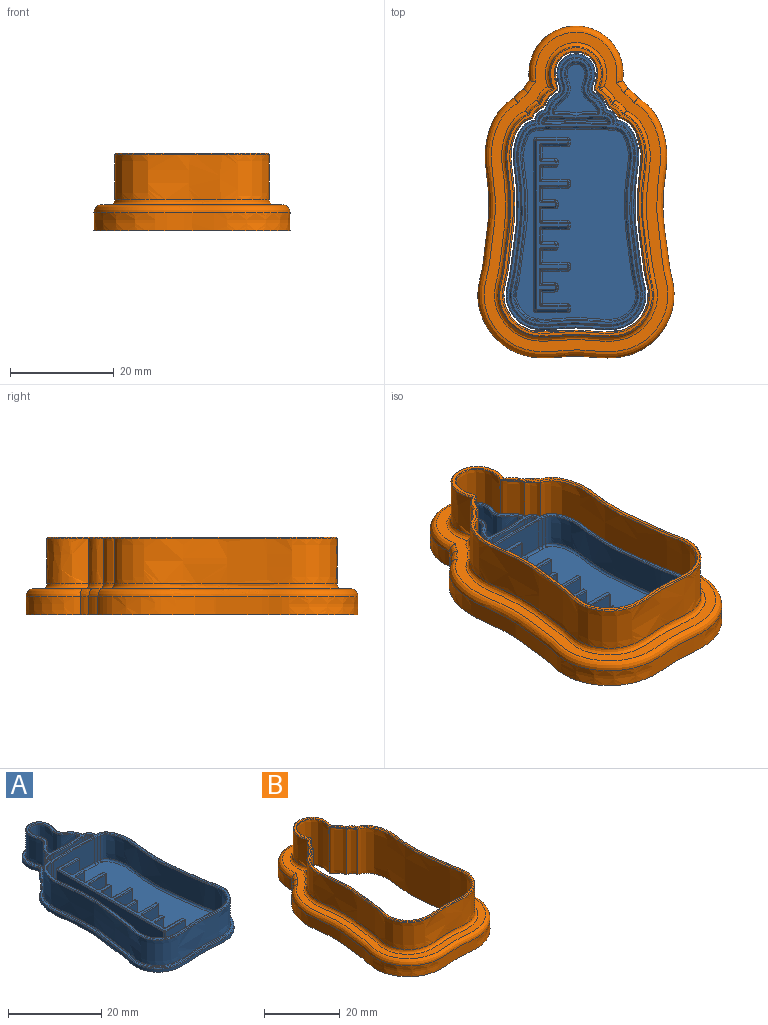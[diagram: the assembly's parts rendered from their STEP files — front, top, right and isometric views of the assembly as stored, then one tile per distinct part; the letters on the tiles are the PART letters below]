
ASSEMBLY  parts=2 mates=1
PART A: 339 faces, bbox 27.6x53.8x8.8 mm
  f0: plane 53.06x26.86mm, normal (0,0,1), area 61.6mm2, adj f215,f216,f217,f218,f219,f220,f221,f222
  f1: extruded ~2.03x1.99mm, area 2.4mm2, adj f2,f4,f5,f227
  f2: extruded ~12.02x10.77mm, area 22.5mm2, adj f1,f3,f5,f229
  f3: extruded ~2.03x1.99mm, area 2.4mm2, adj f2,f4,f5,f230
  f4: extruded ~40.24x26.6mm, area 85.2mm2, adj f1,f3,f5,f228
  f5: plane 53.17x26.93mm, normal (0,0,-1), area 1065.3mm2, adj f1,f2,f3,f4
  f6: extruded ~8.45x6.3mm, area 53.3mm2, adj f115,f118,f206,f234
  f7: extruded ~6.3x0.53mm, area 3.5mm2, adj f8,f118,f203,f235
  f8: extruded ~9.06x8.62mm, area 143.6mm2, adj f7,f37,f205,f233
  f9: extruded ~6.3x0.85mm, area 5.4mm2, adj f10,f34,f214,f334
  f10: extruded ~6.3x0.81mm, area 5.1mm2, adj f9,f11,f213,f333
  f11: extruded ~37.06x23.47mm, area 605.2mm2, adj f10,f12,f211,f335
  f12: extruded ~6.3x0.81mm, area 5.1mm2, adj f11,f13,f209,f337
  f13: extruded ~6.3x0.85mm, area 5.4mm2, adj f12,f34,f210,f338
  f14: extruded ~6.3x0.55mm, area 3.7mm2, adj f35,f116,f201,f242
  f15: extruded ~12.37x6.3mm, area 78mm2, adj f116,f117,f200,f246
  f16: extruded ~6.3x0.55mm, area 3.7mm2, adj f17,f117,f196,f247
  f17: extruded ~6.3x0.31mm, area 2.5mm2, adj f16,f18,f194,f245
  f18: extruded ~6.3x0.78mm, area 5.1mm2, adj f17,f19,f192,f243
  f19: extruded ~6.3x0.81mm, area 5.1mm2, adj f18,f20,f191,f241
  f20: extruded ~8.75x6.3mm, area 55.2mm2, adj f19,f21,f193,f239
  f21: extruded ~6.3x0.81mm, area 5.1mm2, adj f20,f22,f195,f237
  f22: extruded ~6.3x0.78mm, area 5.1mm2, adj f21,f35,f197,f238
  f23: extruded ~6.6x0.79mm, area 5.3mm2, adj f24,f36,f226,f324
  f24: extruded ~38.64x25.05mm, area 666.6mm2, adj f23,f25,f224,f322
  f25: extruded ~6.6x0.79mm, area 5.3mm2, adj f24,f26,f222,f321
  f26: extruded ~6.6x0.81mm, area 5.4mm2, adj f25,f27,f220,f323
  f27: extruded ~6.6x1.1mm, area 10.7mm2, adj f26,f28,f218,f325
  f28: extruded ~6.6x0.8mm, area 5.4mm2, adj f27,f29,f216,f327
  f29: extruded ~6.6x0.81mm, area 5.4mm2, adj f28,f30,f215,f329
  f30: extruded ~10.32x9.87mm, area 166.6mm2, adj f29,f31,f217,f331
  f31: extruded ~6.6x0.81mm, area 5.4mm2, adj f30,f32,f219,f332
  f32: extruded ~6.6x0.8mm, area 5.4mm2, adj f31,f33,f221,f330
  f33: extruded ~6.6x1.1mm, area 10.7mm2, adj f32,f36,f223,f328
  f34: extruded ~12.41x6.3mm, area 78.2mm2, adj f9,f13,f212,f336
  f35: extruded ~6.3x0.31mm, area 2.5mm2, adj f14,f22,f199,f240
  f36: extruded ~6.6x0.81mm, area 5.4mm2, adj f23,f33,f225,f326
  f37: extruded ~6.3x0.53mm, area 3.5mm2, adj f8,f115,f207,f231
  f38: plane 51.56x25.41mm, normal (0,0,1), area 70.5mm2, adj f231,f232,f233,f234,f235,f236,f237,f238
  f39: plane 12.32x0.72mm, normal (0,0,1), area 2.5mm2, adj f191,f192,f193,f194,f195,f196,f197,f199
  f40: plane 36.98x23.4mm, normal (0,0,1), area 599.8mm2, adj f120,f121,f123,f124,f125,f126,f127,f128
  f41: plane 9.88x8.66mm, normal (0,0,1), area 34.3mm2, adj f203,f205,f206,f207
  f42: plane 6.3x4.96mm, normal (0,1,0), area 31.2mm2, adj f79,f82,f172,f295
  f43: plane 6.3x2.56mm, normal (1,0,0), area 16.1mm2, adj f79,f84,f168,f291
  f44: plane 6.3x2.56mm, normal (0,-1,0), area 16.1mm2, adj f84,f85,f164,f287
  f45: plane 6.3x0.48mm, normal (1,0,0), area 3mm2, adj f85,f86,f160,f283
  f46: plane 6.3x2.56mm, normal (0,1,0), area 16.1mm2, adj f83,f86,f156,f279
  f47: plane 6.3x2.56mm, normal (1,0,0), area 16.1mm2, adj f83,f88,f152,f275
  f48: plane 6.3x4.96mm, normal (0,-1,0), area 31.2mm2, adj f88,f89,f148,f271
  f49: plane 6.3x0.48mm, normal (1,0,0), area 3mm2, adj f89,f90,f144,f267
  f50: plane 6.3x4.96mm, normal (0,1,0), area 31.2mm2, adj f87,f90,f140,f263
  f51: plane 6.3x2.56mm, normal (1,0,0), area 16.1mm2, adj f87,f91,f136,f259
  f52: plane 6.3x2.56mm, normal (0,-1,0), area 16.1mm2, adj f91,f93,f132,f255
  f53: plane 6.3x0.48mm, normal (1,0,0), area 3mm2, adj f93,f94,f128,f251
  f54: plane 6.3x2.56mm, normal (0,1,0), area 16.1mm2, adj f92,f94,f124,f250
  f55: plane 6.3x2.56mm, normal (1,0,0), area 16.1mm2, adj f92,f95,f120,f254
  f56: plane 6.3x4.96mm, normal (0,-1,0), area 31.2mm2, adj f95,f97,f121,f258
  f57: plane 6.3x0.48mm, normal (1,0,0), area 3mm2, adj f97,f98,f125,f262
  f58: plane 6.3x4.96mm, normal (0,1,0), area 31.2mm2, adj f96,f98,f129,f266
  f59: plane 6.3x2.56mm, normal (1,0,0), area 16.1mm2, adj f96,f99,f133,f270
  f60: plane 6.3x2.56mm, normal (0,-1,0), area 16.1mm2, adj f99,f101,f137,f274
  f61: plane 6.3x0.48mm, normal (1,0,0), area 3mm2, adj f101,f102,f141,f278
  f62: plane 6.3x2.56mm, normal (0,1,0), area 16.1mm2, adj f100,f102,f145,f282
  f63: plane 6.3x2.56mm, normal (1,0,0), area 16.1mm2, adj f100,f103,f149,f286
  f64: plane 6.3x4.96mm, normal (0,-1,0), area 31.2mm2, adj f103,f105,f153,f290
  f65: plane 6.3x0.48mm, normal (1,0,0), area 3mm2, adj f105,f106,f157,f294
  f66: plane 6.3x4.96mm, normal (0,1,0), area 31.2mm2, adj f104,f106,f161,f298
  f67: plane 6.3x2.56mm, normal (1,0,0), area 16.1mm2, adj f104,f107,f165,f302
  f68: plane 6.3x2.56mm, normal (0,-1,0), area 16.1mm2, adj f107,f109,f169,f306
  f69: plane 6.3x0.48mm, normal (1,0,0), area 3mm2, adj f109,f110,f173,f310
  f70: plane 6.3x2.56mm, normal (0,1,0), area 16.1mm2, adj f108,f110,f177,f314
  f71: plane 6.3x2.56mm, normal (1,0,0), area 16.1mm2, adj f108,f112,f181,f318
  f72: plane 6.3x4.96mm, normal (0,-1,0), area 31.2mm2, adj f112,f113,f185,f319
  f73: plane 6.3x0.48mm, normal (1,0,0), area 3mm2, adj f113,f114,f189,f315
  f74: plane 6.3x5.92mm, normal (0,1,0), area 37.3mm2, adj f111,f114,f188,f311
  f75: plane 32.48x6.3mm, normal (-1,0,0), area 204.6mm2, adj f80,f111,f184,f307
  f76: plane 6.3x5.92mm, normal (0,-1,0), area 37.3mm2, adj f80,f81,f180,f303
  f77: plane 6.3x0.48mm, normal (1,0,0), area 3mm2, adj f81,f82,f176,f299
  f78: plane 32.75x6.19mm, normal (0,0,1), area 46.6mm2, adj f249,f250,f251,f252,f253,f254,f255,f256
  f79: cylinder r=0.24mm len=6.3mm, axis (0,0,1), area 2.4mm2, adj f42,f43,f170,f293
  f80: cylinder r=0.24mm len=6.3mm, axis (0,0,-1), area 2.4mm2, adj f75,f76,f182,f305
  f81: cylinder r=0.24mm len=6.3mm, axis (0,0,-1), area 2.4mm2, adj f76,f77,f178,f301
  f82: cylinder r=0.24mm len=6.3mm, axis (0,0,-1), area 2.4mm2, adj f42,f77,f174,f297
  f83: cylinder r=0.24mm len=6.3mm, axis (0,0,1), area 2.4mm2, adj f46,f47,f154,f277
  f84: cylinder r=0.24mm len=6.3mm, axis (0,0,1), area 2.4mm2, adj f43,f44,f166,f289
  f85: cylinder r=0.24mm len=6.3mm, axis (0,0,-1), area 2.4mm2, adj f44,f45,f162,f285
  f86: cylinder r=0.24mm len=6.3mm, axis (0,0,-1), area 2.4mm2, adj f45,f46,f158,f281
  f87: cylinder r=0.24mm len=6.3mm, axis (0,0,1), area 2.4mm2, adj f50,f51,f138,f261
  f88: cylinder r=0.24mm len=6.3mm, axis (0,0,1), area 2.4mm2, adj f47,f48,f150,f273
  f89: cylinder r=0.24mm len=6.3mm, axis (0,0,-1), area 2.4mm2, adj f48,f49,f146,f269
  f90: cylinder r=0.24mm len=6.3mm, axis (0,0,-1), area 2.4mm2, adj f49,f50,f142,f265
  f91: cylinder r=0.24mm len=6.3mm, axis (0,0,1), area 2.4mm2, adj f51,f52,f134,f257
  f92: cylinder r=0.24mm len=6.3mm, axis (0,0,1), area 2.4mm2, adj f54,f55,f122,f252
  f93: cylinder r=0.24mm len=6.3mm, axis (0,0,-1), area 2.4mm2, adj f52,f53,f130,f253
  f94: cylinder r=0.24mm len=6.3mm, axis (0,0,-1), area 2.4mm2, adj f53,f54,f126,f249
  f95: cylinder r=0.24mm len=6.3mm, axis (0,0,1), area 2.4mm2, adj f55,f56,f119,f256
  f96: cylinder r=0.24mm len=6.3mm, axis (0,0,1), area 2.4mm2, adj f58,f59,f131,f268
  f97: cylinder r=0.24mm len=6.3mm, axis (0,0,-1), area 2.4mm2, adj f56,f57,f123,f260
  f98: cylinder r=0.24mm len=6.3mm, axis (0,0,-1), area 2.4mm2, adj f57,f58,f127,f264
  f99: cylinder r=0.24mm len=6.3mm, axis (0,0,1), area 2.4mm2, adj f59,f60,f135,f272
  f100: cylinder r=0.24mm len=6.3mm, axis (0,0,1), area 2.4mm2, adj f62,f63,f147,f284
  f101: cylinder r=0.24mm len=6.3mm, axis (0,0,-1), area 2.4mm2, adj f60,f61,f139,f276
  f102: cylinder r=0.24mm len=6.3mm, axis (0,0,-1), area 2.4mm2, adj f61,f62,f143,f280
  f103: cylinder r=0.24mm len=6.3mm, axis (0,0,1), area 2.4mm2, adj f63,f64,f151,f288
  f104: cylinder r=0.24mm len=6.3mm, axis (0,0,-1), area 2.4mm2, adj f66,f67,f163,f300
  f105: cylinder r=0.24mm len=6.3mm, axis (0,0,-1), area 2.4mm2, adj f64,f65,f155,f292
  f106: cylinder r=0.24mm len=6.3mm, axis (0,0,1), area 2.4mm2, adj f65,f66,f159,f296
  f107: cylinder r=0.24mm len=6.3mm, axis (0,0,1), area 2.4mm2, adj f67,f68,f167,f304
  f108: cylinder r=0.24mm len=6.3mm, axis (0,0,1), area 2.4mm2, adj f70,f71,f179,f316
  f109: cylinder r=0.24mm len=6.3mm, axis (0,0,-1), area 2.4mm2, adj f68,f69,f171,f308
  f110: cylinder r=0.24mm len=6.3mm, axis (0,0,-1), area 2.4mm2, adj f69,f70,f175,f312
  f111: cylinder r=0.24mm len=6.3mm, axis (0,0,-1), area 2.4mm2, adj f74,f75,f186,f309
  f112: cylinder r=0.24mm len=6.3mm, axis (0,0,1), area 2.4mm2, adj f71,f72,f183,f320
  f113: cylinder r=0.24mm len=6.3mm, axis (0,0,-1), area 2.4mm2, adj f72,f73,f187,f317
  f114: cylinder r=0.24mm len=6.3mm, axis (0,0,-1), area 2.4mm2, adj f73,f74,f190,f313
  f115: cylinder r=0.24mm len=6.3mm, axis (0,0,-1), area 2.5mm2, adj f6,f37,f208,f232
  f116: cylinder r=0.24mm len=6.3mm, axis (0,0,-1), area 2.5mm2, adj f14,f15,f202,f244
  f117: cylinder r=0.24mm len=6.3mm, axis (0,0,-1), area 2.5mm2, adj f15,f16,f198,f248
  f118: cylinder r=0.24mm len=6.3mm, axis (0,0,-1), area 2.5mm2, adj f6,f7,f204,f236
  f119: bspline ~0.5x0.4mm, area 0.1mm2, adj f95,f120,f121
  f120: extruded ~2.56x0.5mm, area 1.7mm2, adj f40,f55,f119,f122
  f121: extruded ~4.96x0.5mm, area 3.5mm2, adj f40,f56,f119,f123
  f122: bspline ~0.5x0.4mm, area 0.1mm2, adj f92,f120,f124
  f123: bspline ~2.08x2.08mm, area 0.4mm2, adj f40,f97,f121,f125
  f124: extruded ~2.56x0.5mm, area 1.8mm2, adj f40,f54,f122,f126
  f125: extruded ~0.5x0.48mm, area 0.3mm2, adj f40,f57,f123,f127
  f126: bspline ~2.08x2.08mm, area 0.4mm2, adj f40,f94,f124,f128
  f127: bspline ~2.08x2.08mm, area 0.4mm2, adj f40,f98,f125,f129
  f128: extruded ~0.5x0.48mm, area 0.3mm2, adj f40,f53,f126,f130
  f129: extruded ~4.96x0.5mm, area 3.5mm2, adj f40,f58,f127,f131
  f130: bspline ~2.08x2.08mm, area 0.4mm2, adj f40,f93,f128,f132
  f131: bspline ~0.5x0.4mm, area 0.1mm2, adj f96,f129,f133
  f132: extruded ~2.56x0.5mm, area 1.8mm2, adj f40,f52,f130,f134
  f133: extruded ~2.56x0.5mm, area 1.7mm2, adj f40,f59,f131,f135
  f134: bspline ~0.5x0.4mm, area 0.1mm2, adj f91,f132,f136
  f135: bspline ~0.5x0.4mm, area 0.1mm2, adj f99,f133,f137
  f136: extruded ~2.56x0.5mm, area 1.7mm2, adj f40,f51,f134,f138
  f137: extruded ~2.56x0.5mm, area 1.8mm2, adj f40,f60,f135,f139
  f138: bspline ~0.5x0.4mm, area 0.1mm2, adj f87,f136,f140
  f139: bspline ~2.08x2.08mm, area 0.4mm2, adj f40,f101,f137,f141
  f140: extruded ~4.96x0.5mm, area 3.5mm2, adj f40,f50,f138,f142
  f141: extruded ~0.5x0.48mm, area 0.3mm2, adj f40,f61,f139,f143
  f142: bspline ~2.08x2.08mm, area 0.4mm2, adj f40,f90,f140,f144
  f143: bspline ~2.08x2.08mm, area 0.4mm2, adj f40,f102,f141,f145
  f144: extruded ~0.5x0.48mm, area 0.3mm2, adj f40,f49,f142,f146
  f145: extruded ~2.56x0.5mm, area 1.8mm2, adj f40,f62,f143,f147
  f146: bspline ~2.08x2.08mm, area 0.4mm2, adj f40,f89,f144,f148
  f147: bspline ~0.5x0.4mm, area 0.1mm2, adj f100,f145,f149
  f148: extruded ~4.96x0.5mm, area 3.5mm2, adj f40,f48,f146,f150
  f149: extruded ~2.56x0.5mm, area 1.7mm2, adj f40,f63,f147,f151
  f150: bspline ~0.5x0.4mm, area 0.1mm2, adj f88,f148,f152
  f151: bspline ~0.5x0.4mm, area 0.1mm2, adj f103,f149,f153
  f152: extruded ~2.56x0.5mm, area 1.7mm2, adj f40,f47,f150,f154
  f153: extruded ~4.96x0.5mm, area 3.5mm2, adj f40,f64,f151,f155
  f154: bspline ~0.5x0.4mm, area 0.1mm2, adj f83,f152,f156
  f155: bspline ~2.08x2.08mm, area 0.4mm2, adj f40,f105,f153,f157
  f156: extruded ~2.56x0.5mm, area 1.8mm2, adj f40,f46,f154,f158
  f157: extruded ~0.5x0.48mm, area 0.3mm2, adj f40,f65,f155,f159
  f158: bspline ~2.08x2.08mm, area 0.4mm2, adj f40,f86,f156,f160
  f159: bspline ~2.08x2.08mm, area 0.4mm2, adj f40,f106,f157,f161
  f160: extruded ~0.5x0.48mm, area 0.3mm2, adj f40,f45,f158,f162
  f161: extruded ~4.96x0.5mm, area 3.5mm2, adj f40,f66,f159,f163
  f162: bspline ~2.08x2.08mm, area 0.4mm2, adj f40,f85,f160,f164
  f163: bspline ~0.5x0.4mm, area 0.1mm2, adj f104,f161,f165
  f164: extruded ~2.56x0.5mm, area 1.8mm2, adj f40,f44,f162,f166
  f165: extruded ~2.56x0.5mm, area 1.7mm2, adj f40,f67,f163,f167
  f166: bspline ~0.5x0.4mm, area 0.1mm2, adj f84,f164,f168
  f167: bspline ~0.5x0.4mm, area 0.1mm2, adj f107,f165,f169
  f168: extruded ~2.56x0.5mm, area 1.7mm2, adj f40,f43,f166,f170
  f169: extruded ~2.56x0.5mm, area 1.8mm2, adj f40,f68,f167,f171
  f170: bspline ~0.5x0.4mm, area 0.1mm2, adj f79,f168,f172
  f171: bspline ~2.08x2.08mm, area 0.4mm2, adj f40,f109,f169,f173
  f172: extruded ~4.96x0.5mm, area 3.5mm2, adj f40,f42,f170,f174
  f173: extruded ~0.5x0.48mm, area 0.3mm2, adj f40,f69,f171,f175
  f174: bspline ~2.08x2.08mm, area 0.4mm2, adj f40,f82,f172,f176
  f175: bspline ~2.08x2.08mm, area 0.4mm2, adj f40,f110,f173,f177
  f176: extruded ~0.5x0.48mm, area 0.3mm2, adj f40,f77,f174,f178
  f177: extruded ~2.56x0.5mm, area 1.8mm2, adj f40,f70,f175,f179
  f178: bspline ~2.08x2.08mm, area 0.4mm2, adj f40,f81,f176,f180
  f179: bspline ~0.5x0.4mm, area 0.1mm2, adj f108,f177,f181
  f180: extruded ~5.92x0.5mm, area 4.2mm2, adj f40,f76,f178,f182
  f181: extruded ~2.56x0.5mm, area 1.7mm2, adj f40,f71,f179,f183
  f182: bspline ~2.08x2.08mm, area 0.4mm2, adj f40,f80,f180,f184
  f183: bspline ~0.5x0.4mm, area 0.1mm2, adj f112,f181,f185
  f184: extruded ~32.48x0.5mm, area 23mm2, adj f40,f75,f182,f186
  f185: extruded ~4.96x0.5mm, area 3.5mm2, adj f40,f72,f183,f187
  f186: bspline ~2.08x2.08mm, area 0.4mm2, adj f40,f111,f184,f188
  f187: bspline ~2.08x2.08mm, area 0.4mm2, adj f40,f113,f185,f189
  f188: extruded ~5.92x0.5mm, area 4.2mm2, adj f40,f74,f186,f190
  f189: extruded ~0.5x0.48mm, area 0.3mm2, adj f40,f73,f187,f190
  f190: bspline ~2.08x2.08mm, area 0.4mm2, adj f40,f114,f188,f189
  f191: bspline ~0.81x0.5mm, area 0.6mm2, adj f19,f39,f192,f193
  f192: bspline ~0.81x0.53mm, area 0.5mm2, adj f18,f39,f191,f194
  f193: bspline ~8.76x0.61mm, area 6.2mm2, adj f20,f39,f191,f195
  f194: bspline ~0.5x0.48mm, area 0.2mm2, adj f17,f39,f192,f196
  f195: bspline ~0.81x0.5mm, area 0.6mm2, adj f21,f39,f193,f197
  f196: bspline ~0.57x0.5mm, area 0.3mm2, adj f16,f39,f194,f198
  f197: bspline ~0.81x0.53mm, area 0.5mm2, adj f22,f39,f195,f199
  f198: bspline ~0.5x0.43mm, area 0.1mm2, adj f117,f196,f200
  f199: bspline ~0.5x0.48mm, area 0.2mm2, adj f35,f39,f197,f201
  f200: bspline ~12.54x0.6mm, area 8.7mm2, adj f15,f39,f198,f202
  f201: bspline ~0.57x0.5mm, area 0.3mm2, adj f14,f39,f199,f202
  f202: bspline ~0.5x0.43mm, area 0.1mm2, adj f116,f200,f201
  f203: bspline ~0.58x0.52mm, area 0.3mm2, adj f7,f41,f204,f205
  f204: bspline ~0.5x0.46mm, area 0.1mm2, adj f118,f203,f206
  f205: bspline ~9.22x8.62mm, area 15.9mm2, adj f8,f41,f203,f207
  f206: bspline ~8.55x0.61mm, area 5.9mm2, adj f6,f41,f204,f208
  f207: bspline ~0.58x0.52mm, area 0.3mm2, adj f37,f41,f205,f208
  f208: bspline ~0.5x0.46mm, area 0.1mm2, adj f115,f206,f207
  f209: bspline ~0.83x0.5mm, area 0.6mm2, adj f12,f40,f210,f211
  f210: bspline ~0.86x0.5mm, area 0.6mm2, adj f13,f40,f209,f212
  f211: bspline ~37.16x23.75mm, area 70.4mm2, adj f11,f40,f209,f213
  f212: bspline ~12.41x0.59mm, area 8.8mm2, adj f34,f40,f210,f214
  f213: bspline ~0.83x0.5mm, area 0.6mm2, adj f10,f40,f211,f214
  f214: bspline ~0.86x0.5mm, area 0.6mm2, adj f9,f40,f212,f213
  f215: bspline ~0.86x0.27mm, area 0.2mm2, adj f0,f29,f216,f217
  f216: bspline ~0.85x0.3mm, area 0.2mm2, adj f0,f28,f215,f218
  f217: bspline ~10.63x10.03mm, area 7.2mm2, adj f0,f30,f215,f219
  f218: bspline ~1.25x1.25mm, area 0.5mm2, adj f0,f27,f216,f220
  f219: bspline ~0.86x0.27mm, area 0.2mm2, adj f0,f31,f217,f221
  f220: bspline ~0.87x0.25mm, area 0.2mm2, adj f0,f26,f218,f222
  f221: bspline ~0.85x0.3mm, area 0.2mm2, adj f0,f32,f219,f223
  f222: bspline ~0.83x0.27mm, area 0.2mm2, adj f0,f25,f220,f224
  f223: bspline ~1.25x1.25mm, area 0.5mm2, adj f0,f33,f221,f225
  f224: bspline ~39.08x25.71mm, area 30.6mm2, adj f0,f24,f222,f226
  f225: bspline ~0.87x0.25mm, area 0.2mm2, adj f0,f36,f223,f226
  f226: bspline ~0.83x0.27mm, area 0.2mm2, adj f0,f23,f224,f225
  f227: bspline ~2.22x2.17mm, area 0.9mm2, adj f0,f1,f228,f229
  f228: bspline ~40.56x26.96mm, area 27.3mm2, adj f0,f4,f227,f230
  f229: bspline ~12.12x11.07mm, area 7.9mm2, adj f0,f2,f227,f230
  f230: bspline ~2.22x2.17mm, area 0.9mm2, adj f0,f3,f228,f229
  f231: bspline ~0.6x0.3mm, area 0.2mm2, adj f37,f38,f232,f233
  f232: bspline ~0.45x0.39mm, area 0.1mm2, adj f38,f115,f231,f234
  f233: bspline ~9.23x8.91mm, area 6.5mm2, adj f8,f38,f231,f235
  f234: bspline ~8.46x0.37mm, area 2.4mm2, adj f6,f38,f232,f236
  f235: bspline ~0.6x0.3mm, area 0.2mm2, adj f7,f38,f233,f236
  f236: bspline ~2.24x1.12mm, area 0.1mm2, adj f38,f118,f234,f235
  f237: bspline ~0.83x0.2mm, area 0.2mm2, adj f21,f38,f238,f239
  f238: bspline ~0.85x0.32mm, area 0.2mm2, adj f22,f38,f237,f240
  f239: bspline ~8.75x0.37mm, area 2.5mm2, adj f20,f38,f237,f241
  f240: bspline ~0.44x0.39mm, area 0.1mm2, adj f35,f38,f238,f242
  f241: bspline ~0.83x0.2mm, area 0.2mm2, adj f19,f38,f239,f243
  f242: bspline ~0.64x0.32mm, area 0.2mm2, adj f14,f38,f240,f244
  f243: bspline ~0.85x0.32mm, area 0.2mm2, adj f18,f38,f241,f245
  f244: bspline ~0.43x0.42mm, area 0.1mm2, adj f38,f116,f242,f246
  f245: bspline ~0.44x0.39mm, area 0.1mm2, adj f17,f38,f243,f247
  f246: bspline ~12.37x0.35mm, area 3.5mm2, adj f15,f38,f244,f248
  f247: bspline ~0.64x0.32mm, area 0.2mm2, adj f16,f38,f245,f248
  f248: bspline ~2.24x1.12mm, area 0.1mm2, adj f38,f117,f246,f247
  f249: bspline ~0.48x0.48mm, area 0.1mm2, adj f78,f94,f250,f251
  f250: extruded ~2.56x0.2mm, area 0.7mm2, adj f54,f78,f249,f252
  f251: extruded ~0.48x0.2mm, area 0.1mm2, adj f53,f78,f249,f253
  f252: bspline ~2.24x1.12mm, area 0.1mm2, adj f78,f92,f250,f254
  f253: bspline ~0.48x0.48mm, area 0.1mm2, adj f78,f93,f251,f255
  f254: extruded ~2.56x0.2mm, area 0.7mm2, adj f55,f78,f252,f256
  f255: extruded ~2.56x0.2mm, area 0.7mm2, adj f52,f78,f253,f257
  f256: bspline ~2.24x1.12mm, area 0.1mm2, adj f78,f95,f254,f258
  f257: bspline ~2.24x1.12mm, area 0.1mm2, adj f78,f91,f255,f259
  f258: extruded ~4.96x0.2mm, area 1.4mm2, adj f56,f78,f256,f260
  f259: extruded ~2.56x0.2mm, area 0.7mm2, adj f51,f78,f257,f261
  f260: bspline ~0.48x0.48mm, area 0.1mm2, adj f78,f97,f258,f262
  f261: bspline ~2.24x1.12mm, area 0.1mm2, adj f78,f87,f259,f263
  f262: extruded ~0.48x0.2mm, area 0.1mm2, adj f57,f78,f260,f264
  f263: extruded ~4.96x0.2mm, area 1.4mm2, adj f50,f78,f261,f265
  f264: bspline ~0.48x0.48mm, area 0.1mm2, adj f78,f98,f262,f266
  f265: bspline ~0.48x0.48mm, area 0.1mm2, adj f78,f90,f263,f267
  f266: extruded ~4.96x0.2mm, area 1.4mm2, adj f58,f78,f264,f268
  f267: extruded ~0.48x0.2mm, area 0.1mm2, adj f49,f78,f265,f269
  f268: bspline ~2.24x1.12mm, area 0.1mm2, adj f78,f96,f266,f270
  f269: bspline ~0.48x0.48mm, area 0.1mm2, adj f78,f89,f267,f271
  f270: extruded ~2.56x0.2mm, area 0.7mm2, adj f59,f78,f268,f272
  f271: extruded ~4.96x0.2mm, area 1.4mm2, adj f48,f78,f269,f273
  f272: bspline ~1.12x1.12mm, area 0.1mm2, adj f78,f99,f270,f274
  f273: bspline ~2.24x1.12mm, area 0.1mm2, adj f78,f88,f271,f275
  f274: extruded ~2.56x0.2mm, area 0.7mm2, adj f60,f78,f272,f276
  f275: extruded ~2.56x0.2mm, area 0.7mm2, adj f47,f78,f273,f277
  f276: bspline ~0.48x0.48mm, area 0.1mm2, adj f78,f101,f274,f278
  f277: bspline ~2.24x1.12mm, area 0.1mm2, adj f78,f83,f275,f279
  f278: extruded ~0.48x0.2mm, area 0.1mm2, adj f61,f78,f276,f280
  f279: extruded ~2.56x0.2mm, area 0.7mm2, adj f46,f78,f277,f281
  f280: bspline ~0.48x0.48mm, area 0.1mm2, adj f78,f102,f278,f282
  f281: bspline ~0.48x0.48mm, area 0.1mm2, adj f78,f86,f279,f283
  f282: extruded ~2.56x0.2mm, area 0.7mm2, adj f62,f78,f280,f284
  f283: extruded ~0.48x0.2mm, area 0.1mm2, adj f45,f78,f281,f285
  f284: bspline ~2.24x1.12mm, area 0.1mm2, adj f78,f100,f282,f286
  f285: bspline ~0.48x0.48mm, area 0.1mm2, adj f78,f85,f283,f287
  f286: extruded ~2.56x0.2mm, area 0.7mm2, adj f63,f78,f284,f288
  f287: extruded ~2.56x0.2mm, area 0.7mm2, adj f44,f78,f285,f289
  f288: bspline ~1.12x1.12mm, area 0.1mm2, adj f78,f103,f286,f290
  f289: bspline ~2.24x1.12mm, area 0.1mm2, adj f78,f84,f287,f291
  f290: extruded ~4.96x0.2mm, area 1.4mm2, adj f64,f78,f288,f292
  f291: extruded ~2.56x0.2mm, area 0.7mm2, adj f43,f78,f289,f293
  f292: bspline ~0.48x0.48mm, area 0.1mm2, adj f78,f105,f290,f294
  f293: bspline ~2.24x1.12mm, area 0.1mm2, adj f78,f79,f291,f295
  f294: extruded ~0.48x0.2mm, area 0.1mm2, adj f65,f78,f292,f296
  f295: extruded ~4.96x0.2mm, area 1.4mm2, adj f42,f78,f293,f297
  f296: bspline ~0.48x0.48mm, area 0.1mm2, adj f78,f106,f294,f298
  f297: bspline ~0.48x0.48mm, area 0.1mm2, adj f78,f82,f295,f299
  f298: extruded ~4.96x0.2mm, area 1.4mm2, adj f66,f78,f296,f300
  f299: extruded ~0.48x0.2mm, area 0.1mm2, adj f77,f78,f297,f301
  f300: bspline ~2.24x1.12mm, area 0.1mm2, adj f78,f104,f298,f302
  f301: bspline ~0.48x0.48mm, area 0.1mm2, adj f78,f81,f299,f303
  f302: extruded ~2.56x0.2mm, area 0.7mm2, adj f67,f78,f300,f304
  f303: extruded ~5.92x0.2mm, area 1.7mm2, adj f76,f78,f301,f305
  f304: bspline ~1.12x1.12mm, area 0.1mm2, adj f78,f107,f302,f306
  f305: bspline ~0.96x0.48mm, area 0.1mm2, adj f78,f80,f303,f307
  f306: extruded ~2.56x0.2mm, area 0.7mm2, adj f68,f78,f304,f308
  f307: extruded ~32.48x0.2mm, area 9.2mm2, adj f75,f78,f305,f309
  f308: bspline ~0.48x0.48mm, area 0.1mm2, adj f78,f109,f306,f310
  f309: bspline ~0.96x0.48mm, area 0.1mm2, adj f78,f111,f307,f311
  f310: extruded ~0.48x0.2mm, area 0.1mm2, adj f69,f78,f308,f312
  f311: extruded ~5.92x0.2mm, area 1.7mm2, adj f74,f78,f309,f313
  f312: bspline ~0.48x0.48mm, area 0.1mm2, adj f78,f110,f310,f314
  f313: bspline ~0.48x0.48mm, area 0.1mm2, adj f78,f114,f311,f315
  f314: extruded ~2.56x0.2mm, area 0.7mm2, adj f70,f78,f312,f316
  f315: extruded ~0.48x0.2mm, area 0.1mm2, adj f73,f78,f313,f317
  f316: bspline ~2.24x1.12mm, area 0.1mm2, adj f78,f108,f314,f318
  f317: bspline ~0.48x0.48mm, area 0.1mm2, adj f78,f113,f315,f319
  f318: extruded ~2.56x0.2mm, area 0.7mm2, adj f71,f78,f316,f320
  f319: extruded ~4.96x0.2mm, area 1.4mm2, adj f72,f78,f317,f320
  f320: bspline ~1.12x1.12mm, area 0.1mm2, adj f78,f112,f318,f319
  f321: bspline ~0.97x0.28mm, area 0.2mm2, adj f25,f38,f322,f323
  f322: bspline ~38.78x25.36mm, area 27.6mm2, adj f24,f38,f321,f324
  f323: bspline ~0.97x0.25mm, area 0.2mm2, adj f26,f38,f321,f325
  f324: bspline ~0.97x0.28mm, area 0.2mm2, adj f23,f38,f322,f326
  f325: bspline ~1.14x1.14mm, area 0.4mm2, adj f27,f38,f323,f327
  f326: bspline ~0.97x0.25mm, area 0.2mm2, adj f36,f38,f324,f328
  f327: bspline ~0.96x0.31mm, area 0.2mm2, adj f28,f38,f325,f329
  f328: bspline ~1.14x1.14mm, area 0.4mm2, adj f33,f38,f326,f330
  f329: bspline ~0.96x0.26mm, area 0.2mm2, adj f29,f38,f327,f331
  f330: bspline ~0.96x0.31mm, area 0.2mm2, adj f32,f38,f328,f332
  f331: bspline ~10.32x9.92mm, area 7.1mm2, adj f30,f38,f329,f332
  f332: bspline ~0.96x0.26mm, area 0.2mm2, adj f31,f38,f330,f331
  f333: bspline ~0.85x0.26mm, area 0.2mm2, adj f10,f38,f334,f335
  f334: bspline ~0.86x0.2mm, area 0.2mm2, adj f9,f38,f333,f336
  f335: bspline ~37.49x24.07mm, area 28.3mm2, adj f11,f38,f333,f337
  f336: bspline ~12.42x0.36mm, area 3.5mm2, adj f34,f38,f334,f338
  f337: bspline ~0.85x0.26mm, area 0.2mm2, adj f12,f38,f335,f338
  f338: bspline ~0.86x0.2mm, area 0.2mm2, adj f13,f38,f336,f337
PART B: 45 faces, bbox 38.4x64.6x15.5 mm
  f0: extruded ~8.75x2.93mm, area 34.6mm2, adj f1,f5,f32,f36
  f1: extruded ~8.75x2.18mm, area 27mm2, adj f0,f2,f31,f38
  f2: extruded ~42.87x29.51mm, area 987.1mm2, adj f1,f3,f29,f37
  f3: extruded ~8.75x2.18mm, area 27mm2, adj f2,f4,f27,f35
  f4: extruded ~8.75x2.86mm, area 34.5mm2, adj f3,f5,f28,f33
  f5: extruded ~10.16x8.75mm, area 192.7mm2, adj f0,f4,f30,f34
  f6: extruded ~14.7x2.08mm, area 45mm2, adj f7,f11,f13,f41
  f7: extruded ~14.85x3.73mm, area 71.2mm2, adj f6,f8,f13,f41,f44
  f8: extruded ~14.85x8.16mm, area 282.1mm2, adj f7,f9,f13,f43
  f9: extruded ~14.85x3.65mm, area 70.1mm2, adj f8,f10,f13,f39,f42
  f10: extruded ~14.7x2.08mm, area 45mm2, adj f9,f11,f13,f39
  f11: extruded ~41.13x27.57mm, area 1595.7mm2, adj f6,f10,f13,f40
  f12: plane 55.87x29.65mm, normal (0,0,1), area 143.5mm2, adj f33,f34,f35,f36,f37,f38,f39,f40
  f13: plane 63.97x37.81mm, normal (0,0,-1), area 783.3mm2, adj f6,f7,f8,f9,f10,f11,f14,f15
  f14: extruded ~3.5x1.81mm, area 8.9mm2, adj f13,f15,f19,f26
  f15: extruded ~3.5x1.63mm, area 7mm2, adj f13,f14,f16,f25
  f16: extruded ~18.17x10.56mm, area 109.9mm2, adj f13,f15,f17,f23
  f17: extruded ~3.5x1.46mm, area 6.3mm2, adj f13,f16,f18,f21
  f18: extruded ~3.5x1.92mm, area 9.4mm2, adj f13,f17,f19,f22
  f19: extruded ~49.96x37.49mm, area 459mm2, adj f13,f14,f18,f24
  f20: plane 62.22x36.07mm, normal (0,0,1), area 304mm2, adj f21,f22,f23,f24,f25,f26,f27,f28
  f21: bspline ~2.74x2.46mm, area 4.5mm2, adj f17,f20,f22,f23
  f22: bspline ~2.98x2.92mm, area 6mm2, adj f18,f20,f21,f24
  f23: bspline ~18.19x11.28mm, area 65mm2, adj f16,f20,f21,f25
  f24: bspline ~50.67x37.84mm, area 276mm2, adj f19,f20,f22,f26
  f25: bspline ~2.88x2.54mm, area 4.9mm2, adj f15,f20,f23,f26
  f26: bspline ~2.9x2.86mm, area 5.7mm2, adj f14,f20,f24,f25
  f27: bspline ~2.96x2.85mm, area 4.2mm2, adj f3,f20,f28,f29
  f28: bspline ~3.62x3.31mm, area 5.2mm2, adj f4,f20,f27,f30
  f29: bspline ~44.62x31.43mm, area 161.3mm2, adj f2,f20,f27,f31
  f30: bspline ~11.8x9.32mm, area 31.8mm2, adj f5,f20,f28,f32
  f31: bspline ~2.96x2.85mm, area 4.2mm2, adj f1,f20,f29,f32
  f32: bspline ~3.68x3.31mm, area 5.2mm2, adj f0,f20,f30,f31
  f33: bspline ~3.38x3.03mm, area 1.3mm2, adj f4,f12,f34,f35
  f34: bspline ~10.22x9.24mm, area 7mm2, adj f5,f12,f33,f36
  f35: bspline ~2.59x2.46mm, area 1mm2, adj f3,f12,f33,f37
  f36: bspline ~3.17x2.79mm, area 1.3mm2, adj f0,f12,f34,f38
  f37: bspline ~43.78x29.85mm, area 36mm2, adj f2,f12,f35,f38
  f38: bspline ~2.37x2.26mm, area 1mm2, adj f1,f12,f36,f37
  f39: bspline ~2.68x2.54mm, area 1.2mm2, adj f9,f10,f12,f40,f42
  f40: bspline ~42.03x28.39mm, area 41.7mm2, adj f11,f12,f39,f41
  f41: bspline ~2.68x2.54mm, area 1.2mm2, adj f6,f7,f12,f40,f44
  f42: bspline ~3.75x2.95mm, area 0.9mm2, adj f9,f12,f39,f43
  f43: bspline ~8.44x7.23mm, area 3.7mm2, adj f8,f12,f42,f44
  f44: bspline ~3.87x2.96mm, area 0.9mm2, adj f7,f12,f41,f43
PLACE A t=(-10.21,5.34,-2.45)mm
PLACE B t=(-9.57,2.71,-2.45)mm
MATE fastened A.f5 <-> B.f13  axis (0,0,-1) through (-10.63,6.03,-2.45)mm
